FCSTD DOCUMENT  (FreeCAD 0.19R24366 (Git))
Label: Amplifier load cell socket and ribbon cable template
License: All rights reserved
LicenseURL: http://en.wikipedia.org/wiki/All_rights_reserved
objects: Sketcher::SketchObject×1, PartDesign::Body×1
note: 2 computed .brp shape members not serialized (recipe doc carries the construction recipe); baked Part::Feature solids carry a one-line shape summary decoded from their .brp

FEATURE [Sketcher::SketchObject] Sketch
  FullyConstrained = true
  MapMode = 5
  Support = -> [XY_Plane]
  sketch-geometry (20):
    g0: Circle CenterX=-13.462 CenterY=22 CenterZ=0 NormalX=0 NormalY=0 NormalZ=1 AngleXU=0 Radius=8
    g1: Circle CenterX=13.462 CenterY=22 CenterZ=0 NormalX=0 NormalY=0 NormalZ=1 AngleXU=0 Radius=8
    g2: LineSegment StartX=-41.1 StartY=0 StartZ=0 EndX=-41.1 EndY=40.5 EndZ=0
    g3: LineSegment StartX=-41.1 StartY=40.5 StartZ=0 EndX=-20 EndY=40.5 EndZ=0
    g4: LineSegment StartX=41.1 StartY=40.5 StartZ=0 EndX=41.1 EndY=0 EndZ=0
    g5: LineSegment StartX=-41.1 StartY=0 StartZ=0 EndX=41.1 EndY=0 EndZ=0
    g6: LineSegment StartX=-20 StartY=40.5 StartZ=0 EndX=-20 EndY=39.2 EndZ=0
    g7: LineSegment StartX=-20 StartY=39.2 StartZ=0 EndX=20 EndY=39.2 EndZ=0
    g8: LineSegment StartX=20 StartY=39.2 StartZ=0 EndX=20 EndY=40.5 EndZ=0
    g9: LineSegment StartX=20 StartY=40.5 StartZ=0 EndX=41.1 EndY=40.5 EndZ=0
    g10: LineSegment StartX=-20 StartY=40.5 StartZ=0 EndX=20 EndY=40.5 EndZ=0
    g11: GeomPoint X=0 Y=11.7 Z=0
    g12: GeomPoint X=0 Y=22 Z=0
    g13: LineSegment StartX=-13.462 StartY=22 StartZ=0 EndX=13.462 EndY=22 EndZ=0
    g14: Circle CenterX=-13.462 CenterY=22 CenterZ=0 NormalX=0 NormalY=0 NormalZ=1 AngleXU=0 Radius=1.35
    g15: Circle CenterX=13.462 CenterY=22 CenterZ=0 NormalX=0 NormalY=0 NormalZ=1 AngleXU=0 Radius=1.35
    g16: LineSegment StartX=-13.462 StartY=30 StartZ=0 EndX=-13.462 EndY=14 EndZ=0
    g17: LineSegment StartX=-21.462 StartY=22 StartZ=0 EndX=-5.462 EndY=22 EndZ=0
    g18: LineSegment StartX=13.462 StartY=30 StartZ=0 EndX=13.462 EndY=14 EndZ=0
    g19: LineSegment StartX=5.462 StartY=22 StartZ=0 EndX=21.462 EndY=22 EndZ=0
  constraints (54):
    c: Symmetric(g0,g1,g-2)
    c: DistanceX(g0,g1) = 26.924
    c: PointOnObject(g2,g-1)
    c: Vertical(g2)
    c: Coincident(g3,g2)
    c: Coincident(g4,g9)
    c: Vertical(g4)
    c: Coincident(g5,g2)
    c: Coincident(g5,g4)
    c: Symmetric(g4,g2,g-2)
    c: DistanceX(g5,g5) = 82.2
    c: DistanceY(g4,g4) = 40.5
    c: Vertical(g6)
    c: Coincident(g7,g6)
    c: Horizontal(g7)
    c: Coincident(g8,g7)
    c: Vertical(g8)
    c: Coincident(g3,g6)
    c: Coincident(g9,g8)
    c: Tangent(g3,g9)
    c: Coincident(g10,g3)
    c: Coincident(g10,g8)
    c: Symmetric(g3,g8,g-2)
    c: DistanceY(g8,g8) = 1.3
    c: DistanceX(g10,g10) = 40
    c: Diameter(g0) = 16
    c: Equal(g1,g0)
    c: PointOnObject(g11,g-2)
    c: DistanceY(g11,g4) = 28.8
    c: PointOnObject(g12,g-2)
    c: Coincident(g13,g0)
    c: Coincident(g13,g1)
    c: PointOnObject(g12,g13)
    c: DistanceY(g11,g1) = 10.3
    c: Coincident(g14,g0)
    c: Coincident(g15,g1)
    c: Equal(g14,g15)
    c: Diameter(g14) = 2.7
    c: PointOnObject(g16,g0)
    c: PointOnObject(g16,g0)
    c: Vertical(g16)
    c: PointOnObject(g17,g0)
    c: PointOnObject(g17,g0)
    c: Horizontal(g17)
    c: PointOnObject(g18,g1)
    c: PointOnObject(g18,g1)
    c: Vertical(g18)
    c: PointOnObject(g19,g1)
    c: PointOnObject(g19,g1)
    c: Horizontal(g19)
    c: PointOnObject(g1,g19)
    c: PointOnObject(g1,g18)
    c: PointOnObject(g0,g17)
    c: PointOnObject(g0,g16)
FEATURE [PartDesign::Body] Body
  Group = -> [Sketch]
  Origin = -> Origin
